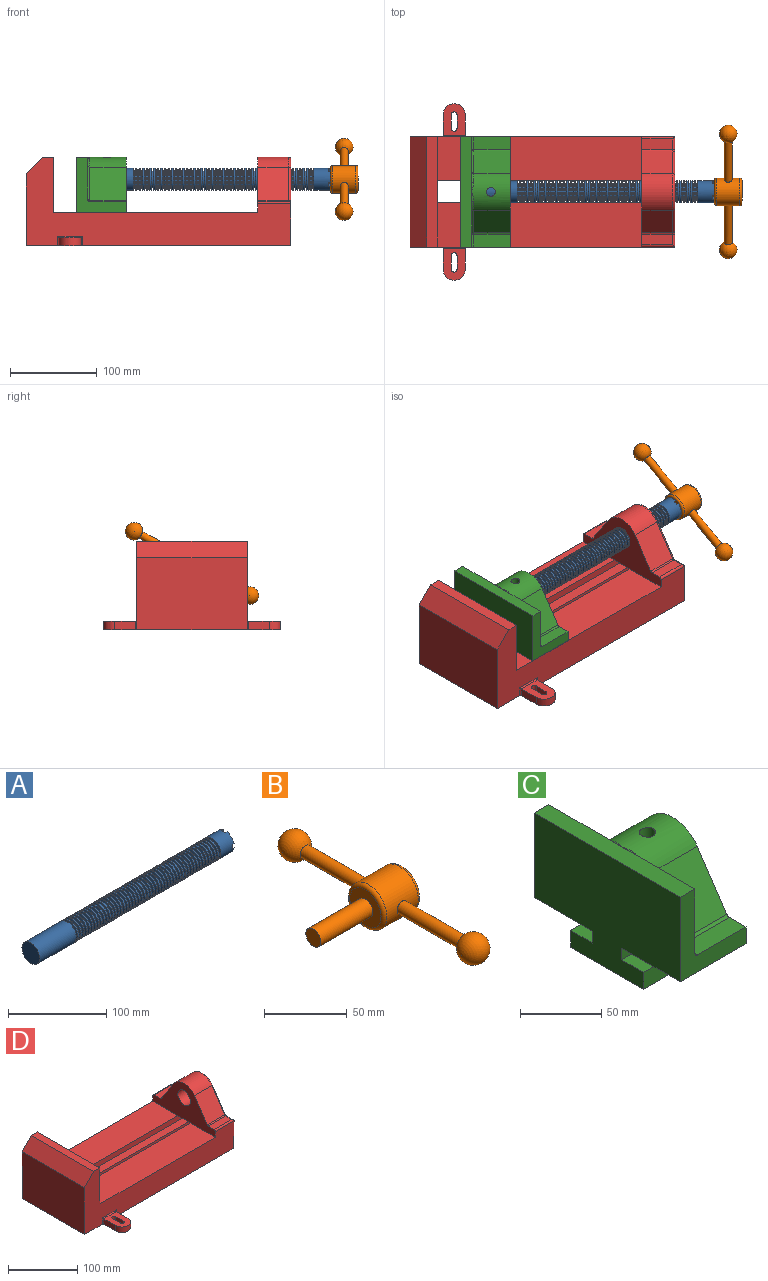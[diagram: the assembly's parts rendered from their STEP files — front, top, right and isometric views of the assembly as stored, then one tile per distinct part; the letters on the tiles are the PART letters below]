
ASSEMBLY  parts=4 mates=3
PART A: 220 faces, bbox 279.4x25.4x25.4 mm
  f0: cylinder r=12.7mm len=25.4mm, axis (-1,0,0), area 1468.2mm2, adj f1,f2,f3,f5,f7,f208,f209,f210
  f1: plane 9.9x9.9mm, normal (1,0,0), area 62.3mm2, adj f0,f4,f213,f216
  f2: plane 9.9x9.9mm, normal (1,0,0), area 62.3mm2, adj f0,f4,f210,f218
  f3: plane 9.9x9.9mm, normal (1,0,0), area 62.3mm2, adj f0,f4,f209,f212
  f4: cylinder r=6.35mm len=25.4mm, axis (1,0,0), area 960.3mm2, adj f1,f2,f3,f5,f6,f208,f209,f210
  f5: plane 9.9x9.9mm, normal (1,0,0), area 62.3mm2, adj f0,f4,f215,f217
  f6: plane 12.7x12.7mm, normal (1,0,0), area 126.7mm2, adj f4
  f7: cone r=12.7mm half-angle=76deg, axis (1,0,0), area 188mm2, adj f0,f9
  f8: cone r=10.16mm half-angle=76deg, axis (-1,0,0), area 188mm2, adj f9,f10
  f9: cylinder r=10.16mm len=20.32mm, axis (1,0,0), area 81.1mm2, adj f7,f8
  f10: cylinder r=12.7mm len=25.4mm, axis (-1,0,0), area 131.7mm2, adj f8,f11
  f11: cone r=12.7mm half-angle=76deg, axis (1,0,0), area 188mm2, adj f10,f13
  f12: cone r=10.16mm half-angle=76deg, axis (-1,0,0), area 188mm2, adj f13,f14
  f13: cylinder r=10.16mm len=20.32mm, axis (1,0,0), area 81.1mm2, adj f11,f12
  f14: cylinder r=12.7mm len=25.4mm, axis (-1,0,0), area 131.7mm2, adj f12,f15
  f15: cone r=12.7mm half-angle=76deg, axis (1,0,0), area 188mm2, adj f14,f17
  f16: cone r=10.16mm half-angle=76deg, axis (-1,0,0), area 188mm2, adj f17,f18
  f17: cylinder r=10.16mm len=20.32mm, axis (1,0,0), area 81.1mm2, adj f15,f16
  f18: cylinder r=12.7mm len=25.4mm, axis (-1,0,0), area 131.7mm2, adj f16,f19
  f19: cone r=12.7mm half-angle=76deg, axis (1,0,0), area 188mm2, adj f18,f21
  f20: cone r=10.16mm half-angle=76deg, axis (-1,0,0), area 188mm2, adj f21,f22
  f21: cylinder r=10.16mm len=20.32mm, axis (1,0,0), area 81.1mm2, adj f19,f20
  f22: cylinder r=12.7mm len=25.4mm, axis (-1,0,0), area 131.7mm2, adj f20,f23
  f23: cone r=12.7mm half-angle=76deg, axis (1,0,0), area 188mm2, adj f22,f25
  f24: cone r=10.16mm half-angle=76deg, axis (-1,0,0), area 188mm2, adj f25,f26
  f25: cylinder r=10.16mm len=20.32mm, axis (1,0,0), area 81.1mm2, adj f23,f24
  f26: cylinder r=12.7mm len=25.4mm, axis (-1,0,0), area 131.7mm2, adj f24,f27
  f27: cone r=12.7mm half-angle=76deg, axis (1,0,0), area 188mm2, adj f26,f29
  f28: cone r=10.16mm half-angle=76deg, axis (-1,0,0), area 188mm2, adj f29,f30
  f29: cylinder r=10.16mm len=20.32mm, axis (1,0,0), area 81.1mm2, adj f27,f28
  f30: cylinder r=12.7mm len=25.4mm, axis (-1,0,0), area 131.7mm2, adj f28,f31
  f31: cone r=12.7mm half-angle=76deg, axis (1,0,0), area 188mm2, adj f30,f33
  f32: cone r=10.16mm half-angle=76deg, axis (-1,0,0), area 188mm2, adj f33,f34
  f33: cylinder r=10.16mm len=20.32mm, axis (1,0,0), area 81.1mm2, adj f31,f32
  f34: cylinder r=12.7mm len=25.4mm, axis (-1,0,0), area 131.7mm2, adj f32,f35
  f35: cone r=12.7mm half-angle=76deg, axis (1,0,0), area 188mm2, adj f34,f37
  f36: cone r=10.16mm half-angle=76deg, axis (-1,0,0), area 188mm2, adj f37,f38
  f37: cylinder r=10.16mm len=20.32mm, axis (1,0,0), area 81.1mm2, adj f35,f36
  f38: cylinder r=12.7mm len=25.4mm, axis (-1,0,0), area 131.7mm2, adj f36,f39
  f39: cone r=12.7mm half-angle=76deg, axis (1,0,0), area 188mm2, adj f38,f41
  f40: cone r=10.16mm half-angle=76deg, axis (-1,0,0), area 188mm2, adj f41,f42
  f41: cylinder r=10.16mm len=20.32mm, axis (1,0,0), area 81.1mm2, adj f39,f40
  f42: cylinder r=12.7mm len=25.4mm, axis (-1,0,0), area 131.7mm2, adj f40,f43
  f43: cone r=12.7mm half-angle=76deg, axis (1,0,0), area 188mm2, adj f42,f45
  f44: cone r=10.16mm half-angle=76deg, axis (-1,0,0), area 188mm2, adj f45,f46
  f45: cylinder r=10.16mm len=20.32mm, axis (1,0,0), area 81.1mm2, adj f43,f44
  f46: cylinder r=12.7mm len=25.4mm, axis (-1,0,0), area 131.7mm2, adj f44,f47
  f47: cone r=12.7mm half-angle=76deg, axis (1,0,0), area 188mm2, adj f46,f49
  f48: cone r=10.16mm half-angle=76deg, axis (-1,0,0), area 188mm2, adj f49,f50
  f49: cylinder r=10.16mm len=20.32mm, axis (1,0,0), area 81.1mm2, adj f47,f48
  f50: cylinder r=12.7mm len=25.4mm, axis (-1,0,0), area 131.7mm2, adj f48,f51
  f51: cone r=12.7mm half-angle=76deg, axis (1,0,0), area 188mm2, adj f50,f53
  f52: cone r=10.16mm half-angle=76deg, axis (-1,0,0), area 188mm2, adj f53,f54
  f53: cylinder r=10.16mm len=20.32mm, axis (1,0,0), area 81.1mm2, adj f51,f52
  f54: cylinder r=12.7mm len=25.4mm, axis (-1,0,0), area 131.7mm2, adj f52,f55
  f55: cone r=12.7mm half-angle=76deg, axis (1,0,0), area 188mm2, adj f54,f57
  f56: cone r=10.16mm half-angle=76deg, axis (-1,0,0), area 188mm2, adj f57,f58
  f57: cylinder r=10.16mm len=20.32mm, axis (1,0,0), area 81.1mm2, adj f55,f56
  f58: cylinder r=12.7mm len=25.4mm, axis (-1,0,0), area 131.7mm2, adj f56,f59
  f59: cone r=12.7mm half-angle=76deg, axis (1,0,0), area 188mm2, adj f58,f61
  f60: cone r=10.16mm half-angle=76deg, axis (-1,0,0), area 188mm2, adj f61,f62
  f61: cylinder r=10.16mm len=20.32mm, axis (1,0,0), area 81.1mm2, adj f59,f60
  f62: cylinder r=12.7mm len=25.4mm, axis (-1,0,0), area 131.7mm2, adj f60,f63
  f63: cone r=12.7mm half-angle=76deg, axis (1,0,0), area 188mm2, adj f62,f65
  f64: cone r=10.16mm half-angle=76deg, axis (-1,0,0), area 188mm2, adj f65,f66
  f65: cylinder r=10.16mm len=20.32mm, axis (1,0,0), area 81.1mm2, adj f63,f64
  f66: cylinder r=12.7mm len=25.4mm, axis (-1,0,0), area 131.7mm2, adj f64,f67
  f67: cone r=12.7mm half-angle=76deg, axis (1,0,0), area 188mm2, adj f66,f69
  f68: cone r=10.16mm half-angle=76deg, axis (-1,0,0), area 188mm2, adj f69,f70
  f69: cylinder r=10.16mm len=20.32mm, axis (1,0,0), area 81.1mm2, adj f67,f68
  f70: cylinder r=12.7mm len=25.4mm, axis (-1,0,0), area 131.7mm2, adj f68,f71
  f71: cone r=12.7mm half-angle=76deg, axis (1,0,0), area 188mm2, adj f70,f73
  f72: cone r=10.16mm half-angle=76deg, axis (-1,0,0), area 188mm2, adj f73,f74
  f73: cylinder r=10.16mm len=20.32mm, axis (1,0,0), area 81.1mm2, adj f71,f72
  f74: cylinder r=12.7mm len=25.4mm, axis (-1,0,0), area 131.7mm2, adj f72,f75
  f75: cone r=12.7mm half-angle=76deg, axis (1,0,0), area 188mm2, adj f74,f77
  f76: cone r=10.16mm half-angle=76deg, axis (-1,0,0), area 188mm2, adj f77,f78
  f77: cylinder r=10.16mm len=20.32mm, axis (1,0,0), area 81.1mm2, adj f75,f76
  f78: cylinder r=12.7mm len=25.4mm, axis (-1,0,0), area 131.7mm2, adj f76,f79
  f79: cone r=12.7mm half-angle=76deg, axis (1,0,0), area 188mm2, adj f78,f81
  f80: cone r=10.16mm half-angle=76deg, axis (-1,0,0), area 188mm2, adj f81,f82
  f81: cylinder r=10.16mm len=20.32mm, axis (1,0,0), area 81.1mm2, adj f79,f80
  f82: cylinder r=12.7mm len=25.4mm, axis (-1,0,0), area 131.7mm2, adj f80,f83
  f83: cone r=12.7mm half-angle=76deg, axis (1,0,0), area 188mm2, adj f82,f85
  f84: cone r=10.16mm half-angle=76deg, axis (-1,0,0), area 188mm2, adj f85,f86
  f85: cylinder r=10.16mm len=20.32mm, axis (1,0,0), area 81.1mm2, adj f83,f84
  f86: cylinder r=12.7mm len=25.4mm, axis (-1,0,0), area 131.7mm2, adj f84,f87
  f87: cone r=12.7mm half-angle=76deg, axis (1,0,0), area 188mm2, adj f86,f89
  f88: cone r=10.16mm half-angle=76deg, axis (-1,0,0), area 188mm2, adj f89,f90
  f89: cylinder r=10.16mm len=20.32mm, axis (1,0,0), area 81.1mm2, adj f87,f88
  f90: cylinder r=12.7mm len=25.4mm, axis (-1,0,0), area 131.7mm2, adj f88,f91
  f91: cone r=12.7mm half-angle=76deg, axis (1,0,0), area 188mm2, adj f90,f93
  f92: cone r=10.16mm half-angle=76deg, axis (-1,0,0), area 188mm2, adj f93,f94
  f93: cylinder r=10.16mm len=20.32mm, axis (1,0,0), area 81.1mm2, adj f91,f92
  f94: cylinder r=12.7mm len=25.4mm, axis (-1,0,0), area 131.7mm2, adj f92,f95
  f95: cone r=12.7mm half-angle=76deg, axis (1,0,0), area 188mm2, adj f94,f97
  f96: cone r=10.16mm half-angle=76deg, axis (-1,0,0), area 188mm2, adj f97,f98
  f97: cylinder r=10.16mm len=20.32mm, axis (1,0,0), area 81.1mm2, adj f95,f96
  f98: cylinder r=12.7mm len=25.4mm, axis (-1,0,0), area 131.7mm2, adj f96,f99
  f99: cone r=12.7mm half-angle=76deg, axis (1,0,0), area 188mm2, adj f98,f101
  f100: cone r=10.16mm half-angle=76deg, axis (-1,0,0), area 188mm2, adj f101,f102
  f101: cylinder r=10.16mm len=20.32mm, axis (1,0,0), area 81.1mm2, adj f99,f100
  f102: cylinder r=12.7mm len=25.4mm, axis (-1,0,0), area 131.7mm2, adj f100,f103
  f103: cone r=12.7mm half-angle=76deg, axis (1,0,0), area 188mm2, adj f102,f105
  f104: cone r=10.16mm half-angle=76deg, axis (-1,0,0), area 188mm2, adj f105,f106
  f105: cylinder r=10.16mm len=20.32mm, axis (1,0,0), area 81.1mm2, adj f103,f104
  f106: cylinder r=12.7mm len=25.4mm, axis (-1,0,0), area 131.7mm2, adj f104,f107
  f107: cone r=12.7mm half-angle=76deg, axis (1,0,0), area 188mm2, adj f106,f109
  f108: cone r=10.16mm half-angle=76deg, axis (-1,0,0), area 188mm2, adj f109,f110
  f109: cylinder r=10.16mm len=20.32mm, axis (1,0,0), area 81.1mm2, adj f107,f108
  f110: cylinder r=12.7mm len=25.4mm, axis (-1,0,0), area 131.7mm2, adj f108,f111
  f111: cone r=12.7mm half-angle=76deg, axis (1,0,0), area 188mm2, adj f110,f113
  f112: cone r=10.16mm half-angle=76deg, axis (-1,0,0), area 188mm2, adj f113,f114
  f113: cylinder r=10.16mm len=20.32mm, axis (1,0,0), area 81.1mm2, adj f111,f112
  f114: cylinder r=12.7mm len=25.4mm, axis (-1,0,0), area 131.7mm2, adj f112,f115
  f115: cone r=12.7mm half-angle=76deg, axis (1,0,0), area 188mm2, adj f114,f117
  f116: cone r=10.16mm half-angle=76deg, axis (-1,0,0), area 188mm2, adj f117,f118
  f117: cylinder r=10.16mm len=20.32mm, axis (1,0,0), area 81.1mm2, adj f115,f116
  f118: cylinder r=12.7mm len=25.4mm, axis (-1,0,0), area 131.7mm2, adj f116,f119
  f119: cone r=12.7mm half-angle=76deg, axis (1,0,0), area 188mm2, adj f118,f121
  f120: cone r=10.16mm half-angle=76deg, axis (-1,0,0), area 188mm2, adj f121,f122
  f121: cylinder r=10.16mm len=20.32mm, axis (1,0,0), area 81.1mm2, adj f119,f120
  f122: cylinder r=12.7mm len=25.4mm, axis (-1,0,0), area 131.7mm2, adj f120,f123
  f123: cone r=12.7mm half-angle=76deg, axis (1,0,0), area 188mm2, adj f122,f125
  f124: cone r=10.16mm half-angle=76deg, axis (-1,0,0), area 188mm2, adj f125,f126
  f125: cylinder r=10.16mm len=20.32mm, axis (1,0,0), area 81.1mm2, adj f123,f124
  f126: cylinder r=12.7mm len=25.4mm, axis (-1,0,0), area 131.7mm2, adj f124,f127
  f127: cone r=12.7mm half-angle=76deg, axis (1,0,0), area 188mm2, adj f126,f129
  f128: cone r=10.16mm half-angle=76deg, axis (-1,0,0), area 188mm2, adj f129,f130
  f129: cylinder r=10.16mm len=20.32mm, axis (1,0,0), area 81.1mm2, adj f127,f128
  f130: cylinder r=12.7mm len=25.4mm, axis (-1,0,0), area 131.7mm2, adj f128,f131
  f131: cone r=12.7mm half-angle=76deg, axis (1,0,0), area 188mm2, adj f130,f133
  f132: cone r=10.16mm half-angle=76deg, axis (-1,0,0), area 188mm2, adj f133,f134
  f133: cylinder r=10.16mm len=20.32mm, axis (1,0,0), area 81.1mm2, adj f131,f132
  f134: cylinder r=12.7mm len=25.4mm, axis (-1,0,0), area 131.7mm2, adj f132,f135
  f135: cone r=12.7mm half-angle=76deg, axis (1,0,0), area 188mm2, adj f134,f137
  f136: cone r=10.16mm half-angle=76deg, axis (-1,0,0), area 188mm2, adj f137,f138
  f137: cylinder r=10.16mm len=20.32mm, axis (1,0,0), area 81.1mm2, adj f135,f136
  f138: cylinder r=12.7mm len=25.4mm, axis (-1,0,0), area 131.7mm2, adj f136,f139
  f139: cone r=12.7mm half-angle=76deg, axis (1,0,0), area 188mm2, adj f138,f141
  f140: cone r=10.16mm half-angle=76deg, axis (-1,0,0), area 188mm2, adj f141,f142
  f141: cylinder r=10.16mm len=20.32mm, axis (1,0,0), area 81.1mm2, adj f139,f140
  f142: cylinder r=12.7mm len=25.4mm, axis (-1,0,0), area 131.7mm2, adj f140,f143
  f143: cone r=12.7mm half-angle=76deg, axis (1,0,0), area 188mm2, adj f142,f145
  f144: cone r=10.16mm half-angle=76deg, axis (-1,0,0), area 188mm2, adj f145,f146
  f145: cylinder r=10.16mm len=20.32mm, axis (1,0,0), area 81.1mm2, adj f143,f144
  f146: cylinder r=12.7mm len=25.4mm, axis (-1,0,0), area 131.7mm2, adj f144,f147
  f147: cone r=12.7mm half-angle=76deg, axis (1,0,0), area 188mm2, adj f146,f149
  f148: cone r=10.16mm half-angle=76deg, axis (-1,0,0), area 188mm2, adj f149,f150
  f149: cylinder r=10.16mm len=20.32mm, axis (1,0,0), area 81.1mm2, adj f147,f148
  f150: cylinder r=12.7mm len=25.4mm, axis (-1,0,0), area 131.7mm2, adj f148,f151
  f151: cone r=12.7mm half-angle=76deg, axis (1,0,0), area 188mm2, adj f150,f153
  f152: cone r=10.16mm half-angle=76deg, axis (-1,0,0), area 188mm2, adj f153,f154
  f153: cylinder r=10.16mm len=20.32mm, axis (1,0,0), area 81.1mm2, adj f151,f152
  f154: cylinder r=12.7mm len=25.4mm, axis (-1,0,0), area 131.7mm2, adj f152,f155
  f155: cone r=12.7mm half-angle=76deg, axis (1,0,0), area 188mm2, adj f154,f157
  f156: cone r=10.16mm half-angle=76deg, axis (-1,0,0), area 188mm2, adj f157,f158
  f157: cylinder r=10.16mm len=20.32mm, axis (1,0,0), area 81.1mm2, adj f155,f156
  f158: cylinder r=12.7mm len=25.4mm, axis (-1,0,0), area 131.7mm2, adj f156,f159
  f159: cone r=12.7mm half-angle=76deg, axis (1,0,0), area 188mm2, adj f158,f161
  f160: cone r=10.16mm half-angle=76deg, axis (-1,0,0), area 188mm2, adj f161,f162
  f161: cylinder r=10.16mm len=20.32mm, axis (1,0,0), area 81.1mm2, adj f159,f160
  f162: cylinder r=12.7mm len=25.4mm, axis (-1,0,0), area 131.7mm2, adj f160,f163
  f163: cone r=12.7mm half-angle=76deg, axis (1,0,0), area 188mm2, adj f162,f165
  f164: cone r=10.16mm half-angle=76deg, axis (-1,0,0), area 188mm2, adj f165,f166
  f165: cylinder r=10.16mm len=20.32mm, axis (1,0,0), area 81.1mm2, adj f163,f164
  f166: cylinder r=12.7mm len=25.4mm, axis (-1,0,0), area 131.7mm2, adj f164,f167
  f167: cone r=12.7mm half-angle=76deg, axis (1,0,0), area 188mm2, adj f166,f169
  f168: cone r=10.16mm half-angle=76deg, axis (-1,0,0), area 188mm2, adj f169,f170
  f169: cylinder r=10.16mm len=20.32mm, axis (1,0,0), area 81.1mm2, adj f167,f168
  f170: cylinder r=12.7mm len=25.4mm, axis (-1,0,0), area 131.7mm2, adj f168,f171
  f171: cone r=12.7mm half-angle=76deg, axis (1,0,0), area 188mm2, adj f170,f173
  f172: cone r=10.16mm half-angle=76deg, axis (-1,0,0), area 188mm2, adj f173,f174
  f173: cylinder r=10.16mm len=20.32mm, axis (1,0,0), area 81.1mm2, adj f171,f172
  f174: cylinder r=12.7mm len=25.4mm, axis (-1,0,0), area 131.7mm2, adj f172,f175
  f175: cone r=12.7mm half-angle=76deg, axis (1,0,0), area 188mm2, adj f174,f177
  f176: cone r=10.16mm half-angle=76deg, axis (-1,0,0), area 188mm2, adj f177,f178
  f177: cylinder r=10.16mm len=20.32mm, axis (1,0,0), area 81.1mm2, adj f175,f176
  f178: cylinder r=12.7mm len=25.4mm, axis (-1,0,0), area 131.7mm2, adj f176,f179
  f179: cone r=12.7mm half-angle=76deg, axis (1,0,0), area 188mm2, adj f178,f181
  f180: cone r=10.16mm half-angle=76deg, axis (-1,0,0), area 188mm2, adj f181,f182
  f181: cylinder r=10.16mm len=20.32mm, axis (1,0,0), area 81.1mm2, adj f179,f180
  f182: cylinder r=12.7mm len=25.4mm, axis (-1,0,0), area 131.7mm2, adj f180,f183
  f183: cone r=12.7mm half-angle=76deg, axis (1,0,0), area 188mm2, adj f182,f185
  f184: cone r=10.16mm half-angle=76deg, axis (-1,0,0), area 188mm2, adj f185,f186
  f185: cylinder r=10.16mm len=20.32mm, axis (1,0,0), area 81.1mm2, adj f183,f184
  f186: cylinder r=12.7mm len=25.4mm, axis (-1,0,0), area 131.7mm2, adj f184,f187
  f187: cone r=12.7mm half-angle=76deg, axis (1,0,0), area 188mm2, adj f186,f189
  f188: cone r=10.16mm half-angle=76deg, axis (-1,0,0), area 188mm2, adj f189,f190
  f189: cylinder r=10.16mm len=20.32mm, axis (1,0,0), area 81.1mm2, adj f187,f188
  f190: cylinder r=12.7mm len=25.4mm, axis (-1,0,0), area 131.7mm2, adj f188,f191
  f191: cone r=12.7mm half-angle=76deg, axis (1,0,0), area 188mm2, adj f190,f193
  f192: cone r=10.16mm half-angle=76deg, axis (-1,0,0), area 188mm2, adj f193,f194
  f193: cylinder r=10.16mm len=20.32mm, axis (1,0,0), area 81.1mm2, adj f191,f192
  f194: cylinder r=12.7mm len=25.4mm, axis (-1,0,0), area 131.7mm2, adj f192,f195
  f195: cone r=12.7mm half-angle=76deg, axis (1,0,0), area 188mm2, adj f194,f197
  f196: cone r=10.16mm half-angle=76deg, axis (-1,0,0), area 188mm2, adj f197,f198
  f197: cylinder r=10.16mm len=20.32mm, axis (1,0,0), area 81.1mm2, adj f195,f196
  f198: cylinder r=12.7mm len=25.4mm, axis (-1,0,0), area 131.7mm2, adj f196,f199
  f199: cone r=12.7mm half-angle=76deg, axis (1,0,0), area 188mm2, adj f198,f201
  f200: cone r=10.16mm half-angle=76deg, axis (-1,0,0), area 188mm2, adj f201,f202
  f201: cylinder r=10.16mm len=20.32mm, axis (1,0,0), area 81.1mm2, adj f199,f200
  f202: cylinder r=12.7mm len=25.4mm, axis (-1,0,0), area 131.7mm2, adj f200,f203
  f203: cone r=12.7mm half-angle=76deg, axis (1,0,0), area 188mm2, adj f202,f205
  f204: cone r=10.16mm half-angle=76deg, axis (-1,0,0), area 188mm2, adj f205,f207
  f205: cylinder r=10.16mm len=20.32mm, axis (1,0,0), area 81.1mm2, adj f203,f204
  f206: plane 25.4x25.4mm, normal (-1,0,0), area 506.7mm2, adj f207
  f207: cylinder r=12.7mm len=52.45mm, axis (-1,0,0), area 4185.4mm2, adj f204,f206
  f208: plane 6.88x5.08mm, normal (1,0,0), area 32.7mm2, adj f0,f4,f209,f210
  f209: plane 6.62x2.54mm, normal (0,-1,0), area 16.8mm2, adj f0,f3,f4,f208
  f210: plane 6.62x2.54mm, normal (0,1,0), area 16.8mm2, adj f0,f2,f4,f208
  f211: plane 6.88x5.08mm, normal (1,0,0), area 32.7mm2, adj f0,f4,f212,f213
  f212: plane 6.62x2.54mm, normal (0,0,1), area 16.8mm2, adj f0,f3,f4,f211
  f213: plane 6.62x2.54mm, normal (0,0,-1), area 16.8mm2, adj f0,f1,f4,f211
  f214: plane 6.88x5.08mm, normal (1,0,0), area 32.7mm2, adj f0,f4,f215,f216
  f215: plane 6.62x2.54mm, normal (0,1,0), area 16.8mm2, adj f0,f4,f5,f214
  f216: plane 6.62x2.54mm, normal (0,-1,0), area 16.8mm2, adj f0,f1,f4,f214
  f217: plane 6.62x2.54mm, normal (0,0,-1), area 16.8mm2, adj f0,f4,f5,f219
  f218: plane 6.62x2.54mm, normal (0,0,1), area 16.8mm2, adj f0,f2,f4,f219
  f219: plane 6.88x5.08mm, normal (1,0,0), area 32.7mm2, adj f0,f4,f217,f218
PART B: 11 faces, bbox 76.2x172.7x34.4 mm
  f0: sphere r=10.16mm, area 1231.8mm2, adj f1
  f1: cylinder r=4.45mm len=51.82mm, axis (0,1,0), area 1438.5mm2, adj f0,f4
  f2: sphere r=10.16mm, area 1231.8mm2, adj f3
  f3: cylinder r=4.45mm len=51.82mm, axis (0,1,0), area 1438.5mm2, adj f2,f4
  f4: cylinder r=15.88mm len=31.75mm, axis (-1,0,0), area 2534.7mm2, adj f1,f3,f9,f10
  f5: cylinder r=6.35mm len=44.45mm, axis (-1,0,0), area 1773.5mm2, adj f6,f8
  f6: plane 12.7x12.7mm, normal (-1,0,0), area 126.7mm2, adj f5
  f7: plane 26.67x26.67mm, normal (1,0,0), area 558.6mm2, adj f10
  f8: plane 26.67x26.67mm, normal (-1,0,0), area 432mm2, adj f5,f9
  f9: torus R=13.33mm, axis (1,0,0), area 374.8mm2, adj f4,f8
  f10: torus R=13.33mm, axis (1,0,0), area 374.8mm2, adj f4,f7
PART C: 36 faces, bbox 57.2x127x89 mm
  f0: plane 57.15x50.8mm, normal (0,0,-1), area 2903.2mm2, adj f6,f9,f10,f23
  f1: cylinder r=12.7mm len=44.45mm, axis (1,0,0), area 3464.3mm2, adj f6,f15,f16
  f2: plane 41.91x14.52mm, normal (0,0,1), area 608.5mm2, adj f6,f11,f24,f25
  f3: plane 51.86x48.26mm, normal (1,0,0), area 1495.7mm2, adj f8,f10,f31,f33,f35
  f4: plane 51.86x48.26mm, normal (1,0,0), area 1495.7mm2, adj f8,f11,f24,f28,f29
  f5: plane 57.15x50.8mm, normal (0,0,-1), area 2903.2mm2, adj f6,f9,f11,f22
  f6: plane 127x85.09mm, normal (1,0,0), area 5190.6mm2, adj f0,f1,f2,f5,f7,f10,f11,f12
  f7: plane 41.91x14.52mm, normal (0,0,1), area 608.5mm2, adj f6,f10,f30,f31
  f8: plane 127x12.7mm, normal (0,0,1), area 1612.9mm2, adj f3,f4,f9,f10,f11,f26,f34
  f9: plane 127x85.09mm, normal (-1,0,0), area 9096.8mm2, adj f0,f5,f8,f10,f11,f17,f18,f19
  f10: plane 63.5x57.15mm, normal (0,-1,0), area 1372.3mm2, adj f0,f3,f6,f7,f8,f9,f31
  f11: plane 63.5x57.15mm, normal (0,1,0), area 1372.3mm2, adj f2,f4,f5,f6,f8,f9,f24
  f12: plane 41.91x38.43mm, normal (0,-0.83,0.56), area 1939.2mm2, adj f6,f13,f30,f33
  f13: cylinder r=25.4mm len=44.45mm, axis (1,0,0), area 2026.5mm2, adj f6,f12,f14,f16,f26,f28,f34,f35
  f14: plane 41.91x38.43mm, normal (0,0.83,0.56), area 1939.2mm2, adj f6,f13,f25,f29
  f15: plane 25.4x25.4mm, normal (1,0,0), area 506.7mm2, adj f1
  f16: cylinder r=5.08mm len=13.76mm, axis (0,0,1), area 414mm2, adj f1,f13
  f17: plane 57.15x19.05mm, normal (0,0,1), area 1088.7mm2, adj f6,f9,f18,f23
  f18: plane 57.15x12.7mm, normal (0,-1,0), area 725.8mm2, adj f6,f9,f17,f19
  f19: plane 63.5x57.15mm, normal (0,0,-1), area 3629mm2, adj f6,f9,f18,f20
  f20: plane 57.15x12.7mm, normal (0,1,0), area 725.8mm2, adj f6,f9,f19,f21
  f21: plane 57.15x19.05mm, normal (0,0,1), area 1088.7mm2, adj f6,f9,f20,f22
  f22: plane 57.15x8.89mm, normal (0,1,0), area 508.1mm2, adj f5,f6,f9,f21
  f23: plane 57.15x8.89mm, normal (0,-1,0), area 508.1mm2, adj f0,f6,f9,f17
  f24: cylinder r=2.54mm len=14.52mm, axis (0,-1,0), area 57.9mm2, adj f2,f4,f11,f27
  f25: cylinder r=2.54mm len=41.91mm, axis (1,0,0), area 104.3mm2, adj f2,f6,f14,f27
  f26: bspline ~12.24x2.8mm, area 20.9mm2, adj f8,f13,f28
  f27: sphere r=2.54mm, area 6.3mm2, adj f24,f25,f29
  f28: torus R=27.94mm, axis (1,0,0), area 57.8mm2, adj f4,f13,f26,f29
  f29: cylinder r=2.54mm len=39.84mm, axis (0,-0.56,0.83), area 184.6mm2, adj f4,f14,f27,f28
  f30: cylinder r=2.54mm len=41.91mm, axis (1,0,0), area 104.3mm2, adj f6,f7,f12,f32
  f31: cylinder r=2.54mm len=14.52mm, axis (0,-1,0), area 57.9mm2, adj f3,f7,f10,f32
  f32: sphere r=2.54mm, area 6.3mm2, adj f30,f31,f33
  f33: cylinder r=2.54mm len=39.84mm, axis (0,-0.56,-0.83), area 184.6mm2, adj f3,f12,f32,f35
  f34: bspline ~12.24x2.8mm, area 20.9mm2, adj f8,f13,f35
  f35: torus R=27.94mm, axis (1,0,0), area 57.8mm2, adj f3,f13,f33,f34
PART D: 61 faces, bbox 304.8x203.2x103.7 mm
  f0: plane 304.8x101.6mm, normal (0,1,0), area 13520.3mm2, adj f3,f4,f5,f6,f7,f8,f9,f16
  f1: plane 304.8x101.6mm, normal (0,-1,0), area 13520.3mm2, adj f2,f3,f5,f6,f7,f8,f9,f16
  f2: plane 234.95x50.8mm, normal (0,0,1), area 11935.5mm2, adj f1,f5,f16,f26
  f3: plane 127x99.06mm, normal (1,0,0), area 7097.5mm2, adj f0,f1,f9,f14,f17,f18,f19,f20
  f4: plane 234.95x50.8mm, normal (0,0,1), area 11935.5mm2, adj f0,f5,f16,f27
  f5: plane 127x101.6mm, normal (1,0,0), area 9516.1mm2, adj f0,f1,f2,f4,f6,f9,f18,f19
  f6: plane 127x12.7mm, normal (0,0,1), area 1612.9mm2, adj f0,f1,f5,f7
  f7: plane 127x19.05mm, normal (-0.71,0,0.71), area 3421.5mm2, adj f0,f1,f6,f8
  f8: plane 127x82.55mm, normal (-1,0,0), area 10483.8mm2, adj f0,f1,f7,f9
  f9: plane 304.8x203.2mm, normal (0,0,-1), area 33298.3mm2, adj f0,f1,f3,f5,f8,f21,f22,f39
  f10: plane 35.56x11.98mm, normal (0,0,1), area 426mm2, adj f16,f28,f29,f30
  f11: plane 38.43x35.56mm, normal (0,0.83,0.56), area 1645.4mm2, adj f12,f16,f29,f32
  f12: cylinder r=25.4mm len=42.19mm, axis (1,0,0), area 1770.2mm2, adj f11,f13,f16,f33
  f13: plane 38.43x35.56mm, normal (0,-0.83,0.56), area 1645.4mm2, adj f12,f16,f34,f35
  f14: cylinder r=12.7mm len=38.1mm, axis (1,0,0), area 3040.2mm2, adj f3,f16
  f15: plane 35.56x11.98mm, normal (0,0,1), area 426mm2, adj f16,f34,f36,f38
  f16: plane 127x63.5mm, normal (-1,0,0), area 4155.5mm2, adj f0,f1,f2,f4,f10,f11,f12,f13
  f17: plane 38.1x25.4mm, normal (0,0,-1), area 967.7mm2, adj f3,f16,f26,f27
  f18: plane 273.05x19.05mm, normal (0,0,-1), area 5201.6mm2, adj f3,f5,f19,f26
  f19: plane 273.05x12.7mm, normal (0,1,0), area 3467.7mm2, adj f3,f5,f18,f20
  f20: plane 273.05x19.05mm, normal (0,0,1), area 5201.6mm2, adj f3,f5,f19,f21
  f21: plane 273.05x16.51mm, normal (0,1,0), area 4508.1mm2, adj f3,f5,f9,f20
  f22: plane 273.05x16.51mm, normal (0,-1,0), area 4508.1mm2, adj f3,f5,f9,f23
  f23: plane 273.05x19.05mm, normal (0,0,1), area 5201.6mm2, adj f3,f5,f22,f24
  f24: plane 273.05x12.7mm, normal (0,-1,0), area 3467.7mm2, adj f3,f5,f23,f25
  f25: plane 273.05x19.05mm, normal (0,0,-1), area 5201.6mm2, adj f3,f5,f24,f27
  f26: plane 273.05x8.89mm, normal (0,1,0), area 2427.4mm2, adj f2,f3,f5,f17,f18
  f27: plane 273.05x8.89mm, normal (0,-1,0), area 2427.4mm2, adj f3,f4,f5,f17,f25
  f28: cylinder r=2.54mm len=38.1mm, axis (1,0,0), area 148.3mm2, adj f0,f10,f16,f30
  f29: cylinder r=2.54mm len=35.56mm, axis (-1,0,0), area 88.5mm2, adj f10,f11,f16,f31
  f30: cylinder r=2.54mm len=14.52mm, axis (0,1,0), area 54.3mm2, adj f3,f10,f28,f31
  f31: torus R=5.08mm, axis (-1,0,0), area 13.5mm2, adj f3,f29,f30,f32
  f32: cylinder r=2.54mm len=39.84mm, axis (0,0.56,-0.83), area 184.6mm2, adj f3,f11,f31,f33
  f33: torus R=22.86mm, axis (-1,0,0), area 191.4mm2, adj f3,f12,f32,f35
  f34: cylinder r=2.54mm len=35.56mm, axis (-1,0,0), area 88.5mm2, adj f13,f15,f16,f37
  f35: cylinder r=2.54mm len=39.84mm, axis (0,0.56,0.83), area 184.6mm2, adj f3,f13,f33,f37
  f36: cylinder r=2.54mm len=38.1mm, axis (-1,0,0), area 148.3mm2, adj f1,f15,f16,f38
  f37: torus R=5.08mm, axis (-1,0,0), area 13.5mm2, adj f3,f34,f35,f38
  f38: cylinder r=2.54mm len=14.52mm, axis (0,1,0), area 54.3mm2, adj f3,f15,f36,f37
  f39: plane 23.88x9.53mm, normal (-1,0,0), area 227.4mm2, adj f9,f45,f46,f60
  f40: plane 23.88x9.53mm, normal (1,0,0), area 227.4mm2, adj f9,f45,f46,f58
  f41: cylinder r=3.3mm len=9.53mm, axis (0,0,-1), area 98.8mm2, adj f9,f42,f44,f46
  f42: plane 15.62x9.53mm, normal (-1,0,0), area 148.8mm2, adj f9,f41,f43,f46
  f43: cylinder r=3.3mm len=9.53mm, axis (0,0,-1), area 98.8mm2, adj f9,f42,f44,f46
  f44: plane 15.62x9.53mm, normal (1,0,0), area 148.8mm2, adj f9,f41,f43,f46
  f45: cylinder r=12.7mm len=25.4mm, axis (0,0,-1), area 380mm2, adj f9,f39,f40,f46
  f46: plane 36.58x25.4mm, normal (0,0,1), area 722.4mm2, adj f39,f40,f41,f42,f43,f44,f45,f59
  f47: plane 23.88x9.53mm, normal (-1,0,0), area 227.4mm2, adj f9,f53,f54,f56
  f48: plane 23.88x9.53mm, normal (1,0,0), area 227.4mm2, adj f9,f53,f54,f55
  f49: cylinder r=3.3mm len=9.53mm, axis (0,0,-1), area 98.8mm2, adj f9,f50,f52,f54
  f50: plane 15.62x9.53mm, normal (-1,0,0), area 148.8mm2, adj f9,f49,f51,f54
  f51: cylinder r=3.3mm len=9.53mm, axis (0,0,-1), area 98.8mm2, adj f9,f50,f52,f54
  f52: plane 15.62x9.53mm, normal (1,0,0), area 148.8mm2, adj f9,f49,f51,f54
  f53: cylinder r=12.7mm len=25.4mm, axis (0,0,-1), area 380mm2, adj f9,f47,f48,f54
  f54: plane 36.58x25.4mm, normal (0,0,1), area 722.4mm2, adj f47,f48,f49,f50,f51,f52,f53,f57
  f55: cylinder r=1.52mm len=11.05mm, axis (0,0,-1), area 24.1mm2, adj f0,f9,f48,f57
  f56: cylinder r=1.52mm len=11.05mm, axis (0,0,1), area 24.1mm2, adj f0,f9,f47,f57
  f57: cylinder r=1.52mm len=28.45mm, axis (1,0,0), area 63.5mm2, adj f0,f54,f55,f56
  f58: cylinder r=1.52mm len=11.05mm, axis (0,0,1), area 24.1mm2, adj f1,f9,f40,f59
  f59: cylinder r=1.52mm len=28.45mm, axis (-1,0,0), area 63.5mm2, adj f1,f46,f58,f60
  f60: cylinder r=1.52mm len=11.05mm, axis (0,0,-1), area 24.1mm2, adj f1,f9,f39,f59
PLACE A rot(axis=(-1,0,0),150.9deg) t=(26.48,-37.05,142.79)mm
PLACE B rot(axis=(-1,0,0),150.9deg) t=(7.43,-37.05,142.79)mm
PLACE C t=(26.48,0,0)mm
PLACE D at identity fixed
MATE fastened A.f4 <-> B.f5  axis (1,0,0) through (45.53,0,76.2)mm
MATE slider C.f9 <-> D.f5  axis (-1,0,0) through (-246.57,-63.5,38.1)mm
MATE cylindrical A.f7 <-> D.f12  axis (-1,0,0) through (-233.87,0,76.2)mm
